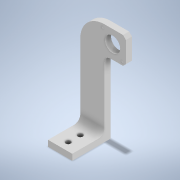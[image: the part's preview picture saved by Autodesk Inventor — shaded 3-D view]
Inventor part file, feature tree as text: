
AUTODESK INVENTOR PART (.ipt)
format: ipt  version: 2020 (Build 240168000, 168)  size: 185,856 bytes
history: native  units: in
note: dims shown in document units (in); Inventor stores cm internally (conversion verified against a paired STEP export)
features: sketch x6, extrude x5, reference x4, fillet x3, other x3, plane x1, chamfer x1
ambient origin geometry x8: Origin, YZ Plane, XZ Plane, XY Plane, X Axis, Y Axis, Z Axis, Center Point
bodies: Solid1 (feature_tree)
feature tree (23):
  sketch  "Sketch1"  dims[d0=0.0in d1=0.0in]
  extrude  "Extrusion1"  TaperAngle=0.0deg  [1 undecoded]
  sketch  "Sketch3"  dims[d10=0.375in d11=2.0in d12=0.0in d13=0.375in]
  plane  "Work Plane1"
  extrude  "Extrusion2"  Depth=0.375in TaperAngle=0.0deg
  extrude  "Extrusion3"  Depth=2.0in TaperAngle=0.0deg
  fillet  "Fillet1"  Radius=0.375in
  extrude  "Extrusion4"  Depth=1.5in
  extrude  "Extrusion5"  Depth=2.0in
  fillet  "Fillet2"  Radius=0.75in
  chamfer  "Chamfer2"  Distance=2.0in
  fillet  "Fillet3"  [1 undecoded]
  sketch  "Sketch2"  dims[d2=0.375in d3=0.0in d8=0.375in d9=0.0in]
  reference  "Reference1"
  reference  "Reference2"
  reference  "Reference3"
  reference  "Reference4"
  sketch  "Sketch4"  dims[d14=1.5in d15=0.3125in]
  sketch  "Sketch5"  dims[d16=0.3125in d17=0.5in d18=0.75in d19=2.0in d20=0.0in d22=0.0in]
  sketch  "Sketch6"  dims[d23=0.0in d24=1.5in d25=2.0in d26=0.0in d27=0.375in d28=0.18in d29=0.125in d30=45.0deg d31=1.5in]
  other  "<userpath>\Desktop\PnP Machine\PnP Machine.iam"
  other  "PnP Machine.iam"
  other  "CUI_DEVICES_AMT132Q-4096-1587:1"
note: 2 required parameter values undecoded (feature->parameter linkage not recoverable at this tier; creation-order binding heuristic only, values carry confidence <= 0.55)
